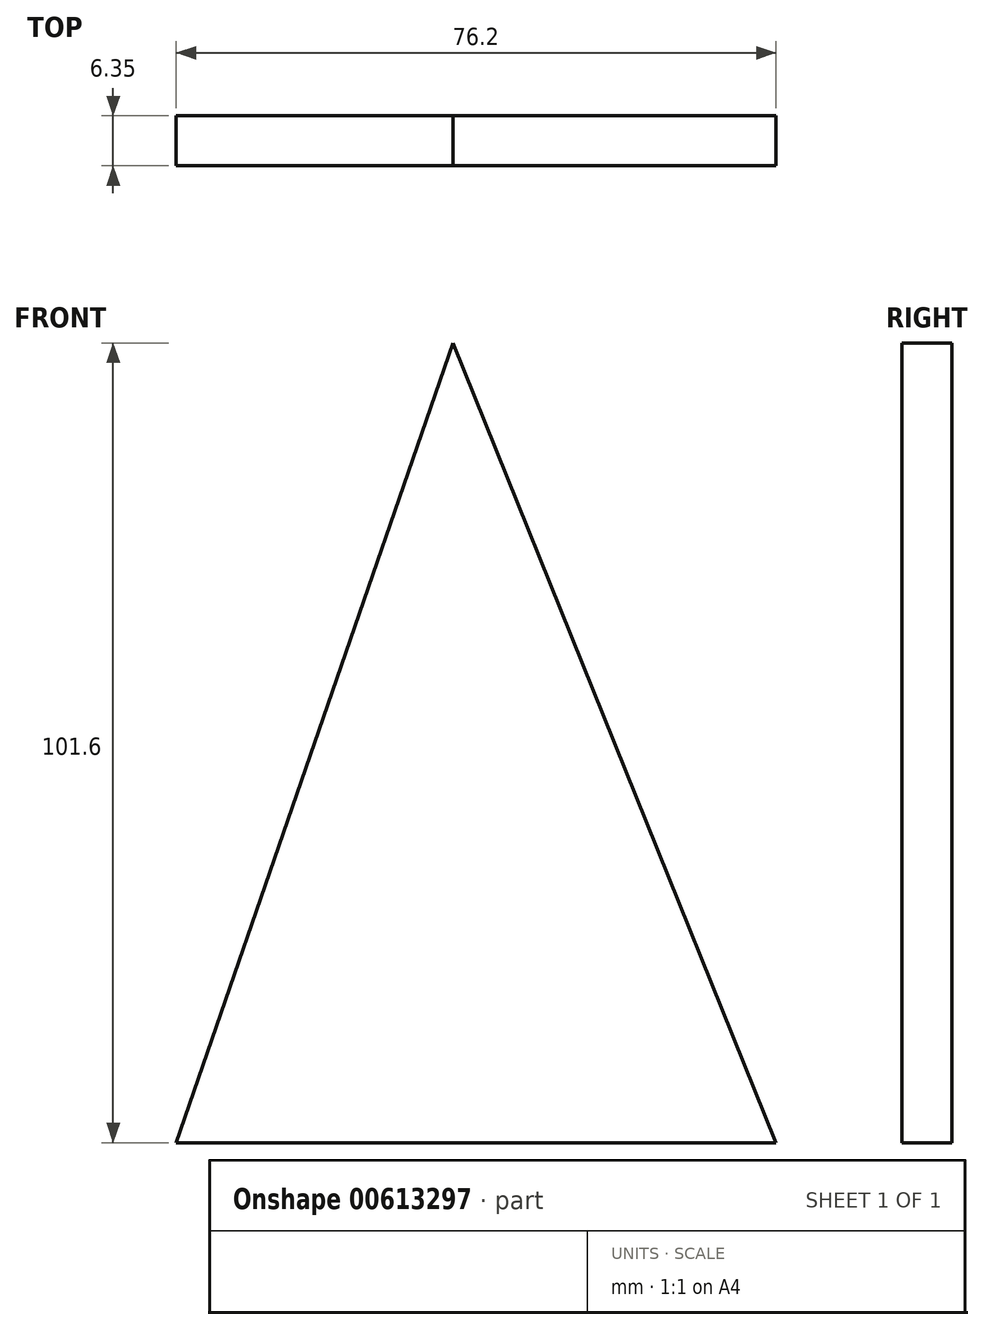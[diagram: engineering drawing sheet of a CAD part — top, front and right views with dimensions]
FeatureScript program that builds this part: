
annotation { "Feature Type Name" : "Feature", "Feature Type Description" : "" }
export const myFeature = defineFeature(function(context is Context, id is Id, definition is map)
    precondition{}
    {
        {
            var Q0;
            Q0=qCreatedBy(makeId("Front.planeOp"),FACE);
            var sketch = newSketch(context, id + "F0", { "sketchPlane" : qUnion([Q0])});
            skLineSegment(sketch, "E0", {"start": v(0, 0) * mm, "end": v(-76.2, 0) * mm});
            skLineSegment(sketch, "E1", {"start": v(-76.2, 0) * mm, "end": v(-41.02, 101.6) * mm});
            skLineSegment(sketch, "E2", {"start": v(-41.02, 101.6) * mm, "end": v(0, 0) * mm});
            skSolve(sketch);
        }
        {
            var Q0;
            Q0=makeQuery(id+"F0.imprint","IMPRINT",FACE,{"disambiguationData":[TD([[makeQuery(id+"F0.imprint","IMPRINT",EDGE,{"derivedFrom":sQuery(id+"F0.wireOp",EDGE,"E0")}),-1.0]])]});
            extrude(context, id + "F1", {"entities" : qUnion([Q0]), "depth" : 6.35 * mm, "offsetDistance" : 25.4 * mm});
        }
    });
